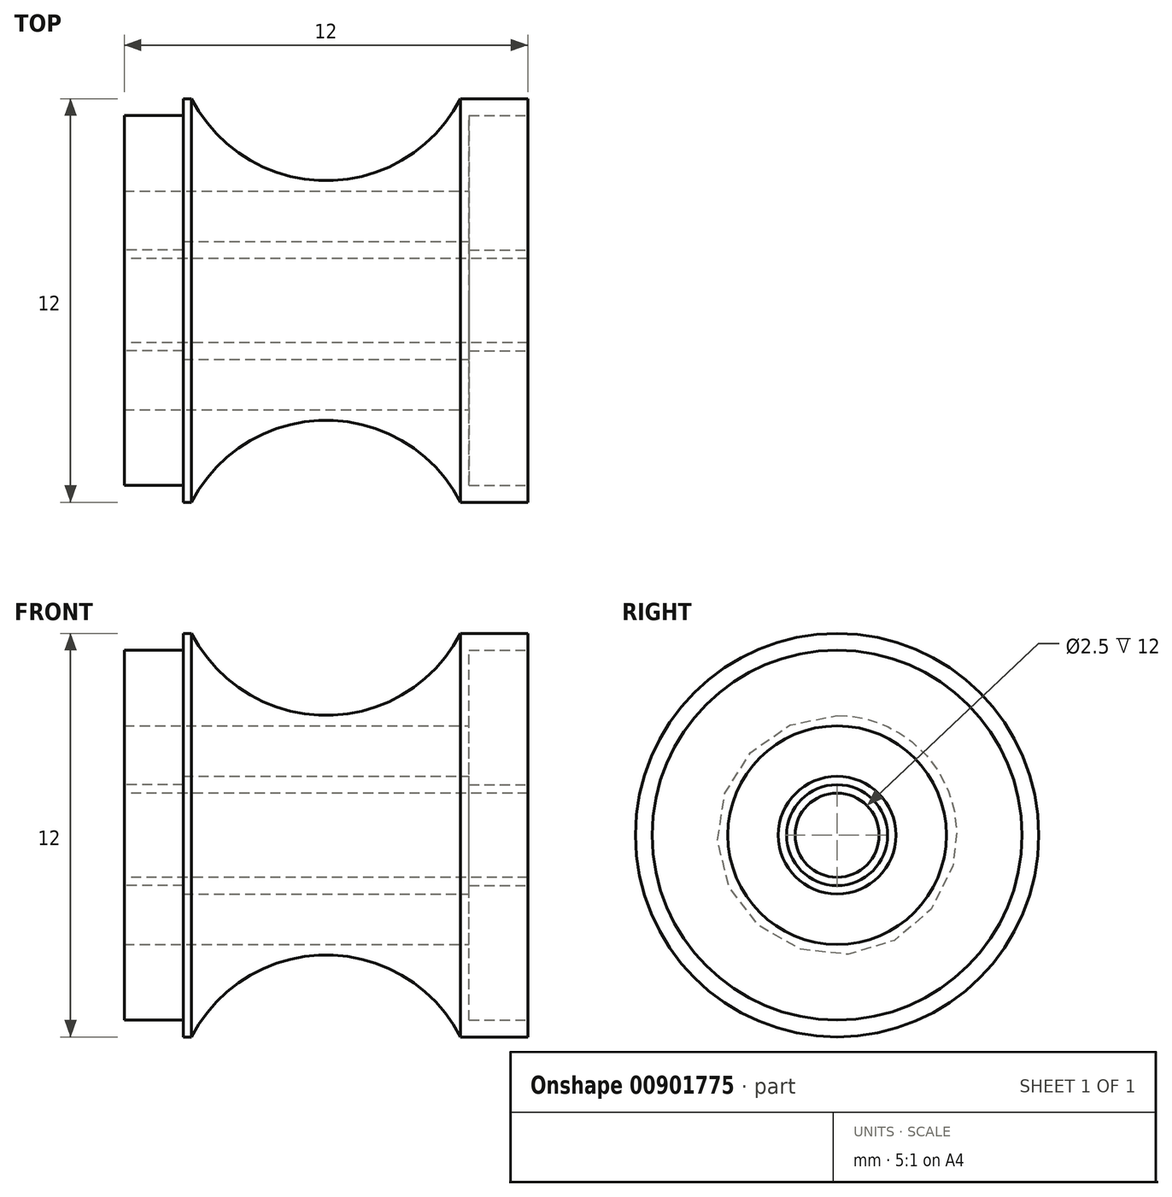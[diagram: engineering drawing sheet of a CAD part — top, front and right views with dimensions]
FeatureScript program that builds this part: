
annotation { "Feature Type Name" : "Feature", "Feature Type Description" : "" }
export const myFeature = defineFeature(function(context is Context, id is Id, definition is map)
    precondition{}
    {
        {
            var Q0;
            Q0=qCreatedBy(makeId("Front.planeOp"),FACE);
            var sketch = newSketch(context, id + "F0", { "sketchPlane" : qUnion([Q0])});
            skLineSegment(sketch, "E0", {"start": v(-5.83, 0) * mm, "end": v(-5.83, 6) * mm});
            skLineSegment(sketch, "E1", {"start": v(-5.83, 6) * mm, "end": v(-3.83, 6) * mm});
            skLineSegment(sketch, "E2", {"start": v(6.17, 0) * mm, "end": v(6.17, 6) * mm});
            skLineSegment(sketch, "E3", {"start": v(6.17, 6) * mm, "end": v(4.17, 6) * mm});
            skArc(sketch, "E4", {"start": v(-3.83, 6) * mm, "mid": v(0.17, 3.56) * mm, "end": v(4.17, 6) * mm});
            skLineSegment(sketch, "E5", {"start": v(-5.83, 0) * mm, "end": v(6.17, 0) * mm});
            skSolve(sketch);
        }
        {
            var Q0;
            Q0 = qSketchRegion(id + "F0", true);
            var Q1;
            Q1=sQuery(id+"F0.wireOp",EDGE,"E5");
            revolve(context, id + "F1", {"surfaceOperationType" : NewSurfaceOperationType.NEW, "entities" : qUnion([Q0]), "axis" : qUnion([Q1]), "revolveType" : RevolveType.FULL});
        }
        {
            var Q0;
            Q0=makeQuery(id+"F1.opRevolve","SWEPT_FACE",FACE,{"disambiguationData":[OSD([sQuery(id+"F0.wireOp",EDGE,"E0")])]});
            var sketch = newSketch(context, id + "F2", { "sketchPlane" : qUnion([Q0])});
            skCircle(sketch, "E6", {"center": v(0, 0) * mm, "radius": 1.25 * mm});
            skSolve(sketch);
        }
        {
            var Q0;
            Q0=makeQuery(id+"F2.imprint","IMPRINT",FACE,{"disambiguationData":[TD([[makeQuery(id+"F2.imprint","IMPRINT",EDGE,{"derivedFrom":sQuery(id+"F2.wireOp",EDGE,"E6")}),1.0]])]});
            extrude(context, id + "F3", {"entities" : qUnion([Q0]), "operationType" : NewBodyOperationType.REMOVE, "endBound" : BoundingType.THROUGH_ALL, "oppositeDirection" : true, "depth" : 12 * mm, "offsetDistance" : 25 * mm});
        }
        {
            var Q0;
            Q0=makeQuery(id+"F1.opRevolve","SWEPT_FACE",FACE,{"disambiguationData":[OSD([sQuery(id+"F0.wireOp",EDGE,"E2")])]});
            var sketch = newSketch(context, id + "F4", { "sketchPlane" : qUnion([Q0])});
            skCircle(sketch, "E7", {"center": v(0, 0) * mm, "radius": 5.5 * mm});
            skCircle(sketch, "E8", {"center": v(0, 0) * mm, "radius": 1.5 * mm});
            skCircle(sketch, "E9", {"center": v(0, 0) * mm, "radius": 3.25 * mm});
            skCircle(sketch, "E10", {"center": v(0, 0) * mm, "radius": 1.75 * mm});
            skSolve(sketch);
        }
        {
            var Q0;
            Q0=makeQuery(id+"F4.imprint","IMPRINT",FACE,{"disambiguationData":[TD([[makeQuery(id+"F4.imprint","IMPRINT",EDGE,{"derivedFrom":sQuery(id+"F4.wireOp",EDGE,"E7")}),1.0]])]});
            extrude(context, id + "F5", {"entities" : qUnion([Q0]), "operationType" : NewBodyOperationType.REMOVE, "oppositeDirection" : true, "depth" : 1.75 * mm, "offsetDistance" : 25 * mm});
        }
        {
            var Q0;
            Q0=makeQuery(id+"F1.opRevolve","SWEPT_FACE",FACE,{"disambiguationData":[OSD([sQuery(id+"F0.wireOp",EDGE,"E0")])]});
            var sketch = newSketch(context, id + "F6", { "sketchPlane" : qUnion([Q0])});
            skCircle(sketch, "E11.0", {"center": v(0, 0) * mm, "radius": 6 * mm});
            skCircle(sketch, "E12.0", {"center": v(0, 0) * mm, "radius": 5.5 * mm});
            skCircle(sketch, "E13.0", {"center": v(0, 0) * mm, "radius": 3.25 * mm});
            skCircle(sketch, "E14.0", {"center": v(0, 0) * mm, "radius": 1.75 * mm});
            skCircle(sketch, "E15.0", {"center": v(0, 0) * mm, "radius": 1.5 * mm});
            skCircle(sketch, "E16.0", {"center": v(0, 0) * mm, "radius": 1.25 * mm});
            skSolve(sketch);
        }
        {
            var Q0;
            Q0=makeQuery(id+"F6.imprint","IMPRINT",FACE,{"disambiguationData":[TD([[makeQuery(id+"F6.imprint","IMPRINT",EDGE,{"derivedFrom":sQuery(id+"F6.wireOp",EDGE,"E12.0")}),-1.0]])]});
            extrude(context, id + "F7", {"entities" : qUnion([Q0]), "operationType" : NewBodyOperationType.REMOVE, "oppositeDirection" : true, "depth" : 1.75 * mm, "offsetDistance" : 25 * mm});
        }
        {
            var Q0;
            Q0=makeQuery(id+"F4.imprint","IMPRINT",FACE,{"disambiguationData":[TD([[makeQuery(id+"F4.imprint","IMPRINT",EDGE,{"derivedFrom":sQuery(id+"F4.wireOp",EDGE,"E9")}),1.0]])]});
            var Q1;
            Q1=sQuery(id+"F4.wireOp",EDGE,"E9");
            var Q2;
            Q2=sQuery(id+"F4.wireOp",EDGE,"E10");
            extrude(context, id + "F8", {"entities" : qUnion([Q0]), "operationType" : NewBodyOperationType.REMOVE, "surfaceEntities" : qUnion([Q1, Q2]), "endBound" : BoundingType.THROUGH_ALL, "oppositeDirection" : true, "depth" : 25 * mm, "offsetDistance" : 25 * mm});
        }
        {
            var Q0;
            Q0=makeQuery(id+"F4.imprint","IMPRINT",FACE,{"disambiguationData":[TD([[makeQuery(id+"F4.imprint","IMPRINT",EDGE,{"derivedFrom":sQuery(id+"F4.wireOp",EDGE,"E8")}),-1.0]])]});
            extrude(context, id + "F9", {"entities" : qUnion([Q0]), "operationType" : NewBodyOperationType.REMOVE, "oppositeDirection" : true, "depth" : 1.75 * mm, "offsetDistance" : 25 * mm});
        }
        {
            var Q0;
            Q0=makeQuery(id+"F7.boolean.opBoolean","SPLIT",FACE,{"disambiguationData":[TD([makeQuery(id+"F3.boolean.opBoolean","COPY",FACE,{"derivedFrom":makeQuery(id+"F3.opExtrude","SWEPT_FACE",FACE,{"disambiguationData":[OSD([sQuery(id+"F2.wireOp",EDGE,"E6")])]})})])],"derivedFrom":makeQuery(id+"F1.opRevolve","SWEPT_FACE",FACE,{"disambiguationData":[OSD([sQuery(id+"F0.wireOp",EDGE,"E0")])]})});
            var sketch = newSketch(context, id + "F10", { "sketchPlane" : qUnion([Q0])});
            skCircle(sketch, "E17.0", {"center": v(0, 0) * mm, "radius": 1.75 * mm});
            skCircle(sketch, "E18.0", {"center": v(0, 0) * mm, "radius": 1.5 * mm});
            skCircle(sketch, "E19.0", {"center": v(0, 0) * mm, "radius": 1.25 * mm});
            skSolve(sketch);
        }
        {
            var Q0;
            Q0=makeQuery(id+"F10.imprint","IMPRINT",FACE,{"disambiguationData":[TD([[makeQuery(id+"F10.imprint","IMPRINT",EDGE,{"derivedFrom":sQuery(id+"F10.wireOp",EDGE,"E17.0")}),1.0]])]});
            extrude(context, id + "F11", {"entities" : qUnion([Q0]), "operationType" : NewBodyOperationType.REMOVE, "oppositeDirection" : true, "depth" : 1.75 * mm, "offsetDistance" : 25 * mm});
        }
    });
